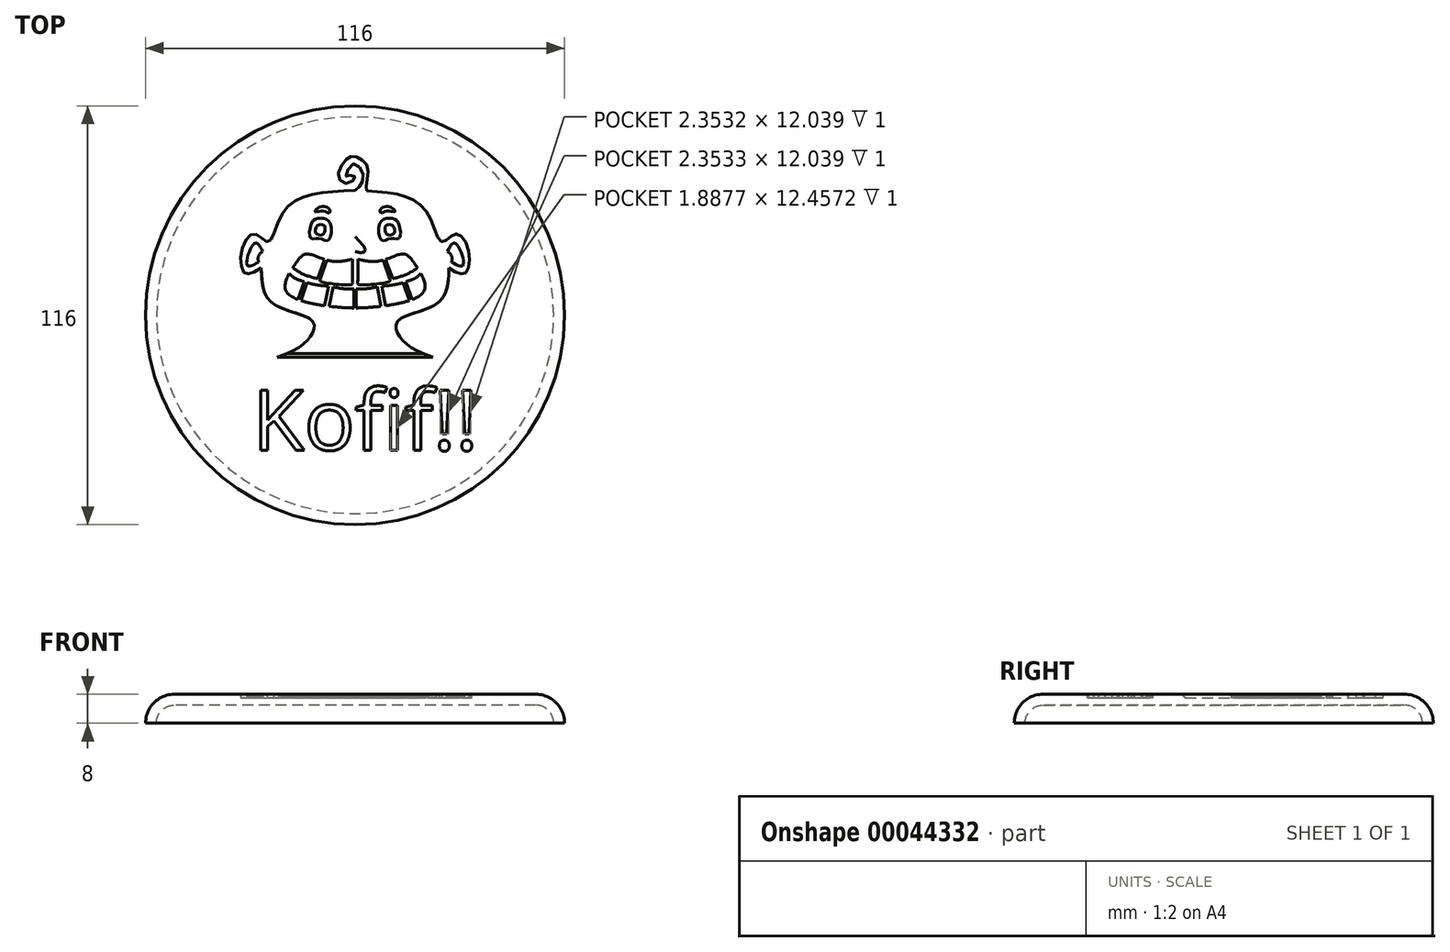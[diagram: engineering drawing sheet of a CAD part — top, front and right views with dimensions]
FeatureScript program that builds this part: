
annotation { "Feature Type Name" : "Feature", "Feature Type Description" : "" }
export const myFeature = defineFeature(function(context is Context, id is Id, definition is map)
    precondition{}
    {
        {
            var Q0;
            Q0=qCreatedBy(makeId("Front.planeOp"),FACE);
            var sketch = newSketch(context, id + "F0", { "sketchPlane" : qUnion([Q0])});
            skLineSegment(sketch, "E0", {"start": v(0, 5) * mm, "end": v(-50, 5) * mm});
            skLineSegment(sketch, "E1", {"start": v(0, 8) * mm, "end": v(-50, 8) * mm});
            skArc(sketch, "E2", {"start": v(-50, 5) * mm, "mid": v(-53.54, 3.54) * mm, "end": v(-55, 0) * mm});
            skArc(sketch, "E3", {"start": v(-50, 8) * mm, "mid": v(-55.66, 5.66) * mm, "end": v(-58, 0) * mm});
            skLineSegment(sketch, "E4", {"start": v(0, 8) * mm, "end": v(0, 5) * mm});
            skLineSegment(sketch, "E5", {"start": v(-58, 0) * mm, "end": v(-55, 0) * mm});
            skSolve(sketch);
        }
        {
            var Q0;
            Q0=qSketchRegion(id+"F0",true);
            var Q1;
            Q1=sQuery(id+"F0.wireOp",EDGE,"E4");
            revolve(context, id + "F1", {"entities" : qUnion([Q0]), "axis" : qUnion([Q1]), "revolveType" : RevolveType.FULL});
        }
        {
            var Q0;
            Q0=makeQuery(id+"F1.opRevolve","SWEPT_FACE",FACE,{"disambiguationData":[OSD([sQuery(id+"F0.wireOp",EDGE,"E1")])]});
            var sketch = newSketch(context, id + "F2", { "sketchPlane" : qUnion([Q0])});
            skText(sketch, "E6", { "text": "Kofif!!", "fontName": "OpenSans-Regular.ttf"});
            skFitSpline(sketch, "E7", {"points": [v(-21.53, -11.6) * mm, v(-12.05, -5.5) * mm, v(-11.93, -1.5) * mm, v(-23.15, 3.61) * mm, v(-26.02, 13.1) * mm], "startDerivative": vector(58.58, 19.87) * mm, "endDerivative": vector(-2.55, 38.94) * mm});
            skFitSpline(sketch, "E8", {"points": [v(-26.02, 13.1) * mm, v(-30.39, 11.6) * mm, v(-31.38, 17.96) * mm, v(-27.77, 22.57) * mm, v(-24.15, 20.32) * mm, v(-20.4, 27.68) * mm, v(-13.05, 33.17) * mm, v(0, 34.54) * mm], "startDerivative": vector(-43.32, -27.23) * mm, "endDerivative": vector(71.84, 2.41) * mm});
            skFitSpline(sketch, "E9.MirrorCS", {"points": [v(21.53, -11.6) * mm, v(12.05, -5.5) * mm, v(11.93, -1.5) * mm, v(23.15, 3.61) * mm, v(26.02, 13.1) * mm], "startDerivative": vector(-58.58, 19.87) * mm, "endDerivative": vector(2.55, 38.94) * mm});
            skFitSpline(sketch, "E10.MirrorCS", {"points": [v(26.02, 13.1) * mm, v(30.39, 11.6) * mm, v(31.38, 17.96) * mm, v(27.77, 22.57) * mm, v(24.15, 20.32) * mm, v(20.4, 27.68) * mm, v(13.05, 33.17) * mm, v(0, 34.54) * mm], "startDerivative": vector(43.32, -27.23) * mm, "endDerivative": vector(-71.84, 2.41) * mm});
            skLineSegment(sketch, "E11", {"start": v(-21.53, -11.6) * mm, "end": v(21.53, -11.6) * mm});
            skFitSpline(sketch, "E12", {"points": [v(0, 34.54) * mm, v(1.8, 36.5) * mm, v(1.9, 40.02) * mm, v(-0.83, 41.8) * mm, v(-2.46, 38.48) * mm, v(-0.83, 38.88) * mm, v(0, 37.94) * mm, v(-2.76, 36.55) * mm, v(-4.64, 39.03) * mm, v(-2.46, 43.14) * mm, v(-0.63, 44.03) * mm, v(1.94, 43.04) * mm, v(3.58, 40.56) * mm, v(3.08, 36.16) * mm, v(3.18, 34.42) * mm], "startDerivative": vector(29.63, 24.42) * mm, "endDerivative": vector(4.8, -26.51) * mm});
            const initialGuessF2  = {"E6": [-0.0284, -0.03737, 1, 0, 0.01676]};
            skSetInitialGuess(sketch, initialGuessF2);
            skSolve(sketch);
        }
        {
            var Q0;
            Q0=qSketchRegion(id+"F2",true);
            extrude(context, id + "F3", {"entities" : qUnion([Q0]), "operationType" : NewBodyOperationType.REMOVE, "oppositeDirection" : true, "depth" : 1 * mm});
        }
        {
            var Q0;
            Q0=makeQuery(id+"F3.boolean.opBoolean","COPY",FACE,{"derivedFrom":makeQuery(id+"F3.opExtrude","CAP_FACE",FACE,{"disambiguationData":[OSD([sQuery(id+"F2.wireOp",EDGE,"E7"),sQuery(id+"F2.wireOp",EDGE,"E8"),sQuery(id+"F2.wireOp",EDGE,"E9.MirrorCS"),sQuery(id+"F2.wireOp",EDGE,"E10.MirrorCS"),sQuery(id+"F2.wireOp",EDGE,"E11"),sQuery(id+"F2.wireOp",EDGE,"E12")])],"isStart":false})});
            var sketch = newSketch(context, id + "F4", { "sketchPlane" : qUnion([Q0])});
            skFitSpline(sketch, "E13", {"points": [v(-15.45, 15.74) * mm, v(-18.95, 6.5) * mm, v(-5.74, 2.33) * mm, v(0, 2) * mm], "startDerivative": vector(-21.9, -30.77) * mm, "endDerivative": vector(17.4, -0.31) * mm});
            skFitSpline(sketch, "E14", {"points": [v(-15.45, 15.74) * mm, v(-14.4, 16.67) * mm, v(-12.68, 16.93) * mm, v(-6.66, 15.01) * mm, v(0, 15.74) * mm], "startDerivative": vector(6.5, 6.16) * mm, "endDerivative": vector(19.19, 5.16) * mm});
            skLineSegment(sketch, "E15", {"start": v(-0.76, 15.54) * mm, "end": v(-0.76, 9.69) * mm});
            skLineSegment(sketch, "E16", {"start": v(-0.76, 9.69) * mm, "end": v(0, 9.69) * mm});
            skLineSegment(sketch, "E17", {"start": v(-8.4, 15.46) * mm, "end": v(-10.4, 10.12) * mm});
            skLineSegment(sketch, "E18", {"start": v(-10.4, 10.12) * mm, "end": v(-9.62, 10.12) * mm});
            skLineSegment(sketch, "E19", {"start": v(-9.62, 10.12) * mm, "end": v(-7.78, 15.27) * mm});
            skLineSegment(sketch, "E20", {"start": v(-15.81, 4.35) * mm, "end": v(-14.03, 9.3) * mm});
            skLineSegment(sketch, "E21", {"start": v(-14.03, 9.3) * mm, "end": v(-13.3, 9.06) * mm});
            skLineSegment(sketch, "E22", {"start": v(-13.3, 9.06) * mm, "end": v(-15, 4.05) * mm});
            skLineSegment(sketch, "E23", {"start": v(-8.46, 2.65) * mm, "end": v(-7.36, 8.07) * mm});
            skLineSegment(sketch, "E24", {"start": v(-7.36, 8.07) * mm, "end": v(-6.1, 7.9) * mm});
            skLineSegment(sketch, "E25", {"start": v(-6.1, 7.9) * mm, "end": v(-7.21, 2.5) * mm});
            skLineSegment(sketch, "E26", {"start": v(0, 7.35) * mm, "end": v(-0.31, 7.35) * mm});
            skLineSegment(sketch, "E27", {"start": v(-0.31, 7.35) * mm, "end": v(-0.31, 2) * mm});
            skFitSpline(sketch, "E28", {"points": [v(-18.21, 11.57) * mm, v(-16.78, 10.32) * mm, v(-14.03, 9.3) * mm], "startDerivative": vector(2.82, -3.03) * mm, "endDerivative": vector(5.44, -1.55) * mm});
            skFitSpline(sketch, "E29", {"points": [v(-13.3, 9.06) * mm, v(-10.77, 8.43) * mm, v(-7.36, 8.07) * mm], "startDerivative": vector(5.2, -1.51) * mm, "endDerivative": vector(6.63, -0.48) * mm});
            skFitSpline(sketch, "E30", {"points": [v(-6.1, 7.9) * mm, v(-3.32, 7.35) * mm, v(-0.31, 7.35) * mm], "startDerivative": vector(5.57, -1.4) * mm, "endDerivative": vector(6, 0.29) * mm});
            skFitSpline(sketch, "E31", {"points": [v(-17.25, 13.14) * mm, v(-14.4, 11.4) * mm, v(-10.4, 10.12) * mm], "startDerivative": vector(5.65, -4.01) * mm, "endDerivative": vector(7.98, -2.05) * mm});
            skFitSpline(sketch, "E32", {"points": [v(-9.62, 10.12) * mm, v(-9.62, 9.5) * mm, v(-5.17, 8.61) * mm, v(-0.76, 8.65) * mm, v(-0.76, 9.69) * mm], "startDerivative": vector(-1.72, -5.08) * mm, "endDerivative": vector(-2.06, 7.15) * mm});
            skLineSegment(sketch, "E33.MirrorCS", {"start": v(14.03, 9.3) * mm, "end": v(13.3, 9.06) * mm});
            skLineSegment(sketch, "E34.MirrorCS", {"start": v(0, 7.35) * mm, "end": v(0.31, 7.35) * mm});
            skLineSegment(sketch, "E35.MirrorCS", {"start": v(10.4, 10.12) * mm, "end": v(9.62, 10.12) * mm});
            skLineSegment(sketch, "E36.MirrorCS", {"start": v(0.76, 9.69) * mm, "end": v(0, 9.69) * mm});
            skFitSpline(sketch, "E37.MirrorCS", {"points": [v(9.62, 10.12) * mm, v(9.62, 9.5) * mm, v(5.17, 8.61) * mm, v(0.76, 8.65) * mm, v(0.76, 9.69) * mm], "startDerivative": vector(1.72, -5.08) * mm, "endDerivative": vector(2.06, 7.15) * mm});
            skLineSegment(sketch, "E38.MirrorCS", {"start": v(9.62, 10.12) * mm, "end": v(7.78, 15.27) * mm});
            skLineSegment(sketch, "E39.MirrorCS", {"start": v(6.1, 7.9) * mm, "end": v(7.21, 2.5) * mm});
            skFitSpline(sketch, "E40.MirrorCS", {"points": [v(6.1, 7.9) * mm, v(3.32, 7.35) * mm, v(0.31, 7.35) * mm], "startDerivative": vector(-5.57, -1.4) * mm, "endDerivative": vector(-6, 0.29) * mm});
            skLineSegment(sketch, "E41.MirrorCS", {"start": v(15.81, 4.35) * mm, "end": v(14.03, 9.3) * mm});
            skLineSegment(sketch, "E42.MirrorCS", {"start": v(0.76, 15.54) * mm, "end": v(0.76, 9.69) * mm});
            skFitSpline(sketch, "E43.MirrorCS", {"points": [v(15.45, 15.74) * mm, v(14.4, 16.67) * mm, v(12.68, 16.93) * mm, v(6.66, 15.01) * mm, v(0, 15.74) * mm], "startDerivative": vector(-6.5, 6.16) * mm, "endDerivative": vector(-19.19, 5.16) * mm});
            skLineSegment(sketch, "E44.MirrorCS", {"start": v(8.4, 15.46) * mm, "end": v(10.4, 10.12) * mm});
            skLineSegment(sketch, "E45.MirrorCS", {"start": v(13.3, 9.06) * mm, "end": v(15, 4.05) * mm});
            skFitSpline(sketch, "E46.MirrorCS", {"points": [v(15.45, 15.74) * mm, v(18.95, 6.5) * mm, v(5.74, 2.33) * mm, v(0, 2) * mm], "startDerivative": vector(21.9, -30.77) * mm, "endDerivative": vector(-17.4, -0.31) * mm});
            skFitSpline(sketch, "E47.MirrorCS", {"points": [v(18.21, 11.57) * mm, v(16.78, 10.32) * mm, v(14.03, 9.3) * mm], "startDerivative": vector(-2.82, -3.03) * mm, "endDerivative": vector(-5.44, -1.55) * mm});
            skLineSegment(sketch, "E48.MirrorCS", {"start": v(0.31, 7.35) * mm, "end": v(0.31, 2) * mm});
            skLineSegment(sketch, "E49.MirrorCS", {"start": v(8.46, 2.65) * mm, "end": v(7.36, 8.07) * mm});
            skLineSegment(sketch, "E50.MirrorCS", {"start": v(7.36, 8.07) * mm, "end": v(6.1, 7.9) * mm});
            skFitSpline(sketch, "E51.MirrorCS", {"points": [v(13.3, 9.06) * mm, v(10.77, 8.43) * mm, v(7.36, 8.07) * mm], "startDerivative": vector(-5.2, -1.51) * mm, "endDerivative": vector(-6.63, -0.48) * mm});
            skFitSpline(sketch, "E52.MirrorCS", {"points": [v(17.25, 13.14) * mm, v(14.4, 11.4) * mm, v(10.4, 10.12) * mm], "startDerivative": vector(-5.65, -4.01) * mm, "endDerivative": vector(-7.98, -2.05) * mm});
            skSolve(sketch);
        }
        {
            var Q0;
            {var subQ1=sQuery(id+"F4.wireOp",EDGE,"E17");Q0=makeQuery(id+"F4.imprint","IMPRINT",FACE,{"disambiguationData":[TD([[makeQuery(id+"F4.imprint","IMPRINT",EDGE,{"derivedFrom":subQ1}),-1.0]])]});}
            var Q1;
            {var subQ1=sQuery(id+"F4.wireOp",EDGE,"E15");Q1=makeQuery(id+"F4.imprint","IMPRINT",FACE,{"disambiguationData":[TD([[makeQuery(id+"F4.imprint","IMPRINT",EDGE,{"derivedFrom":subQ1}),-1.0]])]});}
            var Q2;
            Q2=makeQuery(id+"F4.imprint","IMPRINT",FACE,{"disambiguationData":[TD([[makeQuery(id+"F4.imprint","IMPRINT",EDGE,{"derivedFrom":sQuery(id+"F4.wireOp",EDGE,"E37.MirrorCS")}),-1.0]])]});
            var Q3;
            {var subQ4=sQuery(id+"F4.wireOp",EDGE,"E44.MirrorCS");Q3=makeQuery(id+"F4.imprint","IMPRINT",FACE,{"disambiguationData":[TD([[makeQuery(id+"F4.imprint","IMPRINT",EDGE,{"derivedFrom":subQ4}),1.0]])]});}
            var Q4;
            {var subQ1=sQuery(id+"F4.wireOp",EDGE,"E15");Q4=makeQuery(id+"F4.imprint","IMPRINT",FACE,{"disambiguationData":[TD([[makeQuery(id+"F4.imprint","IMPRINT",EDGE,{"derivedFrom":subQ1}),-1.0]])]});}
            var Q5;
            {var subQ2=sQuery(id+"F4.wireOp",EDGE,"E41.MirrorCS");Q5=makeQuery(id+"F4.imprint","IMPRINT",FACE,{"disambiguationData":[TD([[makeQuery(id+"F4.imprint","IMPRINT",EDGE,{"derivedFrom":subQ2}),-1.0]])]});}
            var Q6;
            {var subQ2=sQuery(id+"F4.wireOp",EDGE,"E45.MirrorCS");Q6=makeQuery(id+"F4.imprint","IMPRINT",FACE,{"disambiguationData":[TD([[makeQuery(id+"F4.imprint","IMPRINT",EDGE,{"derivedFrom":subQ2}),-1.0]])]});}
            var Q7;
            {var subQ2=sQuery(id+"F4.wireOp",EDGE,"E39.MirrorCS");Q7=makeQuery(id+"F4.imprint","IMPRINT",FACE,{"disambiguationData":[TD([[makeQuery(id+"F4.imprint","IMPRINT",EDGE,{"derivedFrom":subQ2}),-1.0]])]});}
            var Q8;
            {var subQ1=sQuery(id+"F4.wireOp",EDGE,"E25");Q8=makeQuery(id+"F4.imprint","IMPRINT",FACE,{"disambiguationData":[TD([[makeQuery(id+"F4.imprint","IMPRINT",EDGE,{"derivedFrom":subQ1}),1.0]])]});}
            var Q9;
            {var subQ1=sQuery(id+"F4.wireOp",EDGE,"E22");Q9=makeQuery(id+"F4.imprint","IMPRINT",FACE,{"disambiguationData":[TD([[makeQuery(id+"F4.imprint","IMPRINT",EDGE,{"derivedFrom":subQ1}),1.0]])]});}
            var Q10;
            {var subQ0=sQuery(id+"F4.wireOp",EDGE,"E20");Q10=makeQuery(id+"F4.imprint","IMPRINT",FACE,{"disambiguationData":[TD([[makeQuery(id+"F4.imprint","IMPRINT",EDGE,{"derivedFrom":subQ0}),1.0]])]});}
            extrude(context, id + "F5", {"entities" : qUnion([Q0, Q1, Q2, Q3, Q4, Q5, Q6, Q7, Q8, Q9, Q10]), "operationType" : NewBodyOperationType.ADD, "depth" : 0.5 * mm});
        }
        {
            var Q0;
            Q0=makeQuery(id+"F3.boolean.opBoolean","COPY",FACE,{"derivedFrom":makeQuery(id+"F3.opExtrude","CAP_FACE",FACE,{"disambiguationData":[OSD([sQuery(id+"F2.wireOp",EDGE,"E7"),sQuery(id+"F2.wireOp",EDGE,"E8"),sQuery(id+"F2.wireOp",EDGE,"E9.MirrorCS"),sQuery(id+"F2.wireOp",EDGE,"E10.MirrorCS"),sQuery(id+"F2.wireOp",EDGE,"E11"),sQuery(id+"F2.wireOp",EDGE,"E12")])],"isStart":false})});
            var sketch = newSketch(context, id + "F6", { "sketchPlane" : qUnion([Q0])});
            skFitSpline(sketch, "E53", {"points": [v(-9.56, 26.88) * mm, v(-11.76, 25.96) * mm, v(-12.26, 21.38) * mm, v(-9.85, 21.26) * mm, v(-7.35, 20.8) * mm, v(-6.94, 25.67) * mm, v(-9.56, 26.88) * mm]});
            skFitSpline(sketch, "E54", {"points": [v(-7.14, 28.37) * mm, v(-8.85, 28.87) * mm, v(-11.06, 28.7) * mm, v(-10.52, 29.54) * mm, v(-8.68, 30.12) * mm, v(-7.02, 29.29) * mm, v(-7.14, 28.37) * mm]});
            skFitSpline(sketch, "E55", {"points": [v(-9.5, 25.15) * mm, v(-10.62, 24.64) * mm, v(-10.9, 22.86) * mm, v(-9.73, 22.2) * mm, v(-8.7, 22.54) * mm, v(-8.43, 24.64) * mm, v(-9.5, 25.15) * mm]});
            skFitSpline(sketch, "E56.MirrorC", {"points": [v(7.14, 28.37) * mm, v(8.85, 28.87) * mm, v(11.06, 28.7) * mm, v(10.52, 29.54) * mm, v(8.68, 30.12) * mm, v(7.02, 29.29) * mm, v(7.14, 28.37) * mm]});
            skFitSpline(sketch, "E57.MirrorC", {"points": [v(9.56, 26.88) * mm, v(11.76, 25.96) * mm, v(12.26, 21.38) * mm, v(9.85, 21.26) * mm, v(7.35, 20.8) * mm, v(6.94, 25.67) * mm, v(9.56, 26.88) * mm]});
            skFitSpline(sketch, "E58.MirrorC", {"points": [v(9.5, 25.15) * mm, v(10.62, 24.64) * mm, v(10.9, 22.86) * mm, v(9.73, 22.2) * mm, v(8.7, 22.54) * mm, v(8.43, 24.64) * mm, v(9.5, 25.15) * mm]});
            skFitSpline(sketch, "E59", {"points": [v(25.61, 17.68) * mm, v(27.77, 19.97) * mm, v(29.9, 13.92) * mm, v(26.74, 14.68) * mm], "startDerivative": vector(6.9, 14.1) * mm, "endDerivative": vector(-14.2, 8) * mm});
            skFitSpline(sketch, "E60", {"points": [v(25.61, 17.68) * mm, v(26.74, 16.44) * mm, v(26.74, 14.68) * mm], "startDerivative": vector(2.84, -2.27) * mm, "endDerivative": vector(-0.58, -3.72) * mm});
            skFitSpline(sketch, "E61.MirrorCS", {"points": [v(-25.61, 17.68) * mm, v(-26.74, 16.44) * mm, v(-26.74, 14.68) * mm], "startDerivative": vector(-2.84, -2.27) * mm, "endDerivative": vector(0.58, -3.72) * mm});
            skFitSpline(sketch, "E62.MirrorCS", {"points": [v(-25.61, 17.68) * mm, v(-27.77, 19.97) * mm, v(-29.9, 13.92) * mm, v(-26.74, 14.68) * mm], "startDerivative": vector(-6.9, 14.1) * mm, "endDerivative": vector(14.2, 8) * mm});
            skFitSpline(sketch, "E63", {"points": [v(0, 21.75) * mm, v(-2.8, 18.02) * mm, v(-1.74, 17.36) * mm, v(0, 17.72) * mm], "startDerivative": vector(-9.37, -9.44) * mm, "endDerivative": vector(5.98, 2.11) * mm});
            skFitSpline(sketch, "E64.MirrorCS", {"points": [v(0, 21.75) * mm, v(2.8, 18.02) * mm, v(1.74, 17.36) * mm, v(0, 17.72) * mm], "startDerivative": vector(9.37, -9.44) * mm, "endDerivative": vector(-5.98, 2.11) * mm});
            skSolve(sketch);
        }
        {
            var Q0;
            Q0 = qSketchRegion(id + "F6", true);
            extrude(context, id + "F7", {"entities" : qUnion([Q0]), "operationType" : NewBodyOperationType.ADD, "depth" : 0.5 * mm});
        }
        {
            var Q0;
            Q0=makeQuery(id+"F3.boolean.opBoolean","COPY",EDGE,{"derivedFrom":makeQuery(id+"F3.opExtrude","CAP_EDGE",EDGE,{"disambiguationData":[OSD([sQuery(id+"F2.wireOp",EDGE,"E11")])],"isStart":false})});
            chamfer(context, id + "F8", {"entities" : qUnion([Q0]), "width" : 1 * mm, "tangentPropagation" : true});
        }
    });
